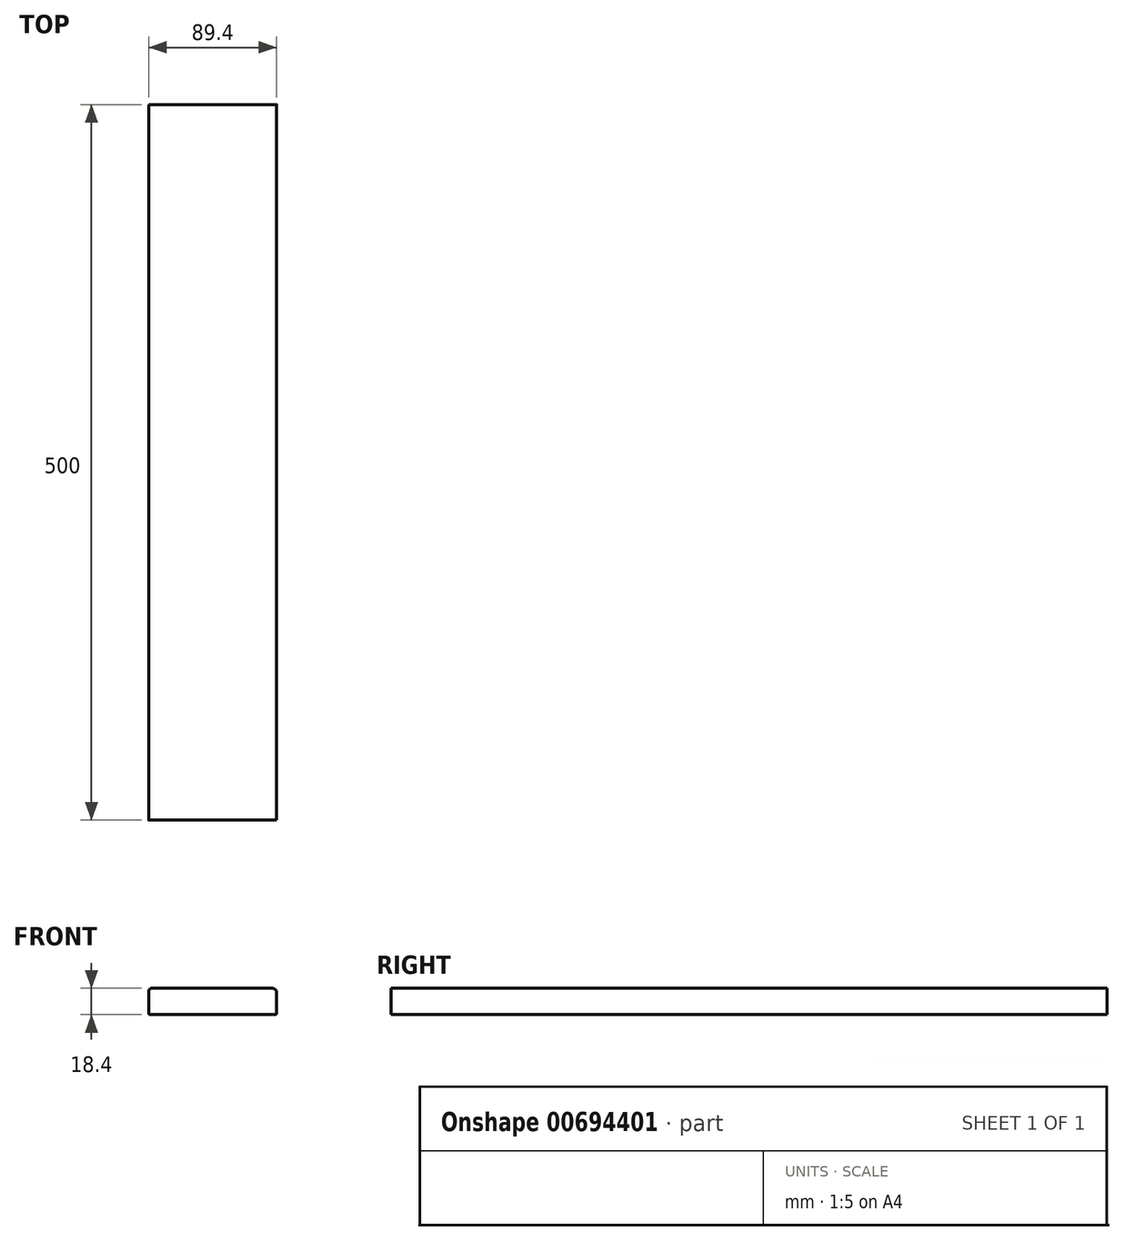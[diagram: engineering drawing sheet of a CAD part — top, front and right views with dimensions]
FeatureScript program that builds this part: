
annotation { "Feature Type Name" : "Feature", "Feature Type Description" : "" }
export const myFeature = defineFeature(function(context is Context, id is Id, definition is map)
    precondition{}
    {
        {
            var Q0;
            Q0=qCreatedBy(makeId("Front.planeOp"),FACE);
            var sketch = newSketch(context, id + "F0", { "sketchPlane" : qUnion([Q0])});
            skLineSegment(sketch, "E0", {"start": v(-65.1, 26.3) * mm, "end": v(19.9, 26.3) * mm});
            skLineSegment(sketch, "E1", {"start": v(22.9, 23.3) * mm, "end": v(22.9, 8.3) * mm});
            skLineSegment(sketch, "E2", {"start": v(21.9, 7.3) * mm, "end": v(17.1, 7.3) * mm});
            skLineSegment(sketch, "E3", {"start": v(-67.1, 8.3) * mm, "end": v(-67.1, 24.3) * mm});
            skPoint(sketch, "E4.visualSharp", {"position": v(-67.1, 26.3) * mm});
            skArc(sketch, "E4.filletArc", {"start": v(-65.1, 26.3) * mm, "mid": v(-66.51, 25.7) * mm, "end": v(-67.1, 24.3) * mm});
            skPoint(sketch, "E5.visualSharp", {"position": v(22.9, 26.3) * mm});
            skArc(sketch, "E5.filletArc", {"start": v(22.9, 23.3) * mm, "mid": v(22.02, 25.42) * mm, "end": v(19.9, 26.3) * mm});
            skArc(sketch, "E6.filletArc", {"start": v(-67.1, 8.3) * mm, "mid": v(-66.8, 7.59) * mm, "end": v(-66.1, 7.3) * mm});
            skPoint(sketch, "E7.visualSharp", {"position": v(22.9, 7.3) * mm});
            skArc(sketch, "E7.filletArc", {"start": v(21.9, 7.3) * mm, "mid": v(22.6, 7.59) * mm, "end": v(22.9, 8.3) * mm});
            skLineSegment(sketch, "E8.0", {"start": v(-64.8, 26) * mm, "end": v(19.6, 26) * mm});
            skLineSegment(sketch, "E8.1", {"start": v(-66.8, 8.6) * mm, "end": v(-66.8, 24) * mm});
            skLineSegment(sketch, "E8.2", {"start": v(21.6, 7.6) * mm, "end": v(-65.8, 7.6) * mm});
            skLineSegment(sketch, "E8.3", {"start": v(22.6, 23) * mm, "end": v(22.6, 8.6) * mm});
            skPoint(sketch, "E9.visualSharp", {"position": v(-66.8, 26) * mm});
            skArc(sketch, "E9.filletArc", {"start": v(-64.8, 26) * mm, "mid": v(-66.21, 25.4) * mm, "end": v(-66.8, 24) * mm});
            skPoint(sketch, "E10.visualSharp", {"position": v(-66.8, 7.6) * mm});
            skArc(sketch, "E10.filletArc", {"start": v(-66.8, 8.6) * mm, "mid": v(-66.5, 7.89) * mm, "end": v(-65.8, 7.6) * mm});
            skPoint(sketch, "E11.visualSharp", {"position": v(22.6, 7.6) * mm});
            skArc(sketch, "E11.filletArc", {"start": v(21.6, 7.6) * mm, "mid": v(22.3, 7.89) * mm, "end": v(22.6, 8.6) * mm});
            skPoint(sketch, "E12.visualSharp", {"position": v(22.6, 26) * mm});
            skArc(sketch, "E12.filletArc", {"start": v(22.6, 23) * mm, "mid": v(21.72, 25.12) * mm, "end": v(19.6, 26) * mm});
            skLineSegment(sketch, "E13", {"start": v(-57.8, 7.3) * mm, "end": v(-57.8, 7.6) * mm});
            skLineSegment(sketch, "E14", {"start": v(17.1, 7.3) * mm, "end": v(17.1, 7.6) * mm});
            skLineSegment(sketch, "E15.trimOffspring", {"start": v(-57.8, 7.3) * mm, "end": v(-66.1, 7.3) * mm});
            skSolve(sketch);
        }
        {
            var Q0;
            Q0=makeQuery(id+"F0.imprint","IMPRINT",FACE,{"disambiguationData":[TD([[makeQuery(id+"F0.imprint","IMPRINT",EDGE,{"derivedFrom":sQuery(id+"F0.wireOp",EDGE,"E8.0")}),-1.0]])]});
            extrude(context, id + "F1", {"entities" : qUnion([Q0]), "depth" : 500 * mm, "offsetDistance" : 25 * mm});
        }
    });
